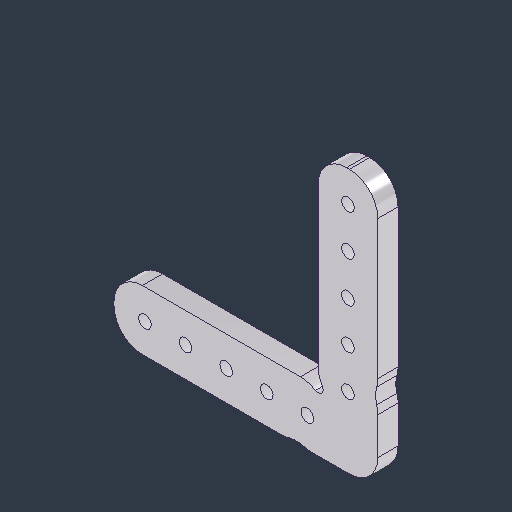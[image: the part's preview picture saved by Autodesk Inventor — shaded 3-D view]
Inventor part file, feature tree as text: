
AUTODESK INVENTOR PART (.ipt)
format: ipt  version: 2024.3 (Build 283343000, 343)  size: 239,616 bytes
history: native  units: in
note: dims shown in document units (in); Inventor stores cm internally (conversion verified against a paired STEP export)
features: sketch x2, other x2, sheet_metal_op x1, hole x1, pattern_circular x1, chamfer x1
ambient origin geometry x8: Origin, YZ Plane, XZ Plane, XY Plane, X Axis, Y Axis, Z Axis, Center Point
bodies: Solid1 (feature_tree)
feature tree (8):
  sketch  "Sketch1"  dims[d1=0.735in d2=3.25in]
  sheet_metal_op  "Face1"
  hole  "Hole3"  [1 undecoded]
  pattern_circular  "Circular Pattern1"  [2 undecoded]
  chamfer  "Corner Round1"
  other  "Plate1"
  sketch  "Sketch3"  dims[d14=1.0in d32=0.25in d33=0.8675in d34=1.9685in d36=0.5in d37=0.3937in d39=1.0in d41=0.156in d42=0.38in d43=0.375in d44=0.25in d45=0.5635in d46=1.0in d47=0.8108in d48=0.0625in d49=0.7874in d50=90.0deg d52=0.35in d53=0.0in d54=0.0in d55=0.0in d56=0.0in d57=0.3125in d58=0.68in d59=1.0in]
  other  "Definition1"
note: 3 required parameter values undecoded (feature->parameter linkage not recoverable at this tier; creation-order binding heuristic only, values carry confidence <= 0.55)
